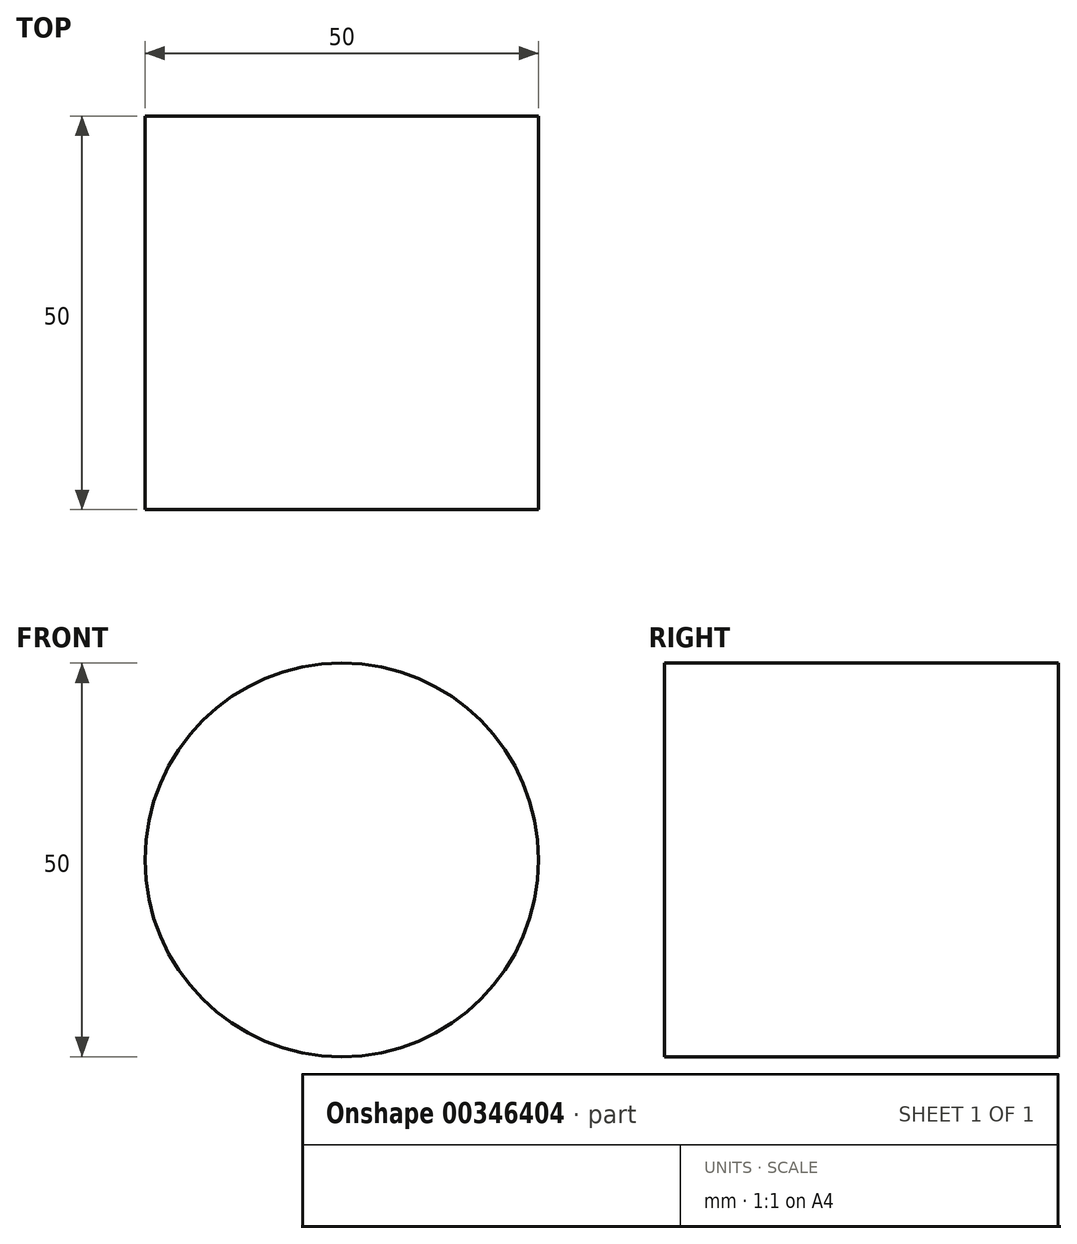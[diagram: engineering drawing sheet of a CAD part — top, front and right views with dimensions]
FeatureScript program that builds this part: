
annotation { "Feature Type Name" : "Feature", "Feature Type Description" : "" }
export const myFeature = defineFeature(function(context is Context, id is Id, definition is map)
    precondition{}
    {
        {
            var Q0;
            Q0=qCreatedBy(makeId("Front.planeOp"),FACE);
            var sketch = newSketch(context, id + "F0", { "sketchPlane" : qUnion([Q0])});
            skCircle(sketch, "E0", {"center": v(0, 0) * mm, "radius": 25 * mm});
            skSolve(sketch);
        }
        {
            var Q0;
            Q0 = qSketchRegion(id + "F0", true);
            extrude(context, id + "F1", {"entities" : qUnion([Q0]), "flatOperationType" : FlatOperationType.REMOVE, "offsetDistance" : 25 * mm, "depth" : 50 * mm, "domain" : OperationDomain.MODEL});
        }
    });
